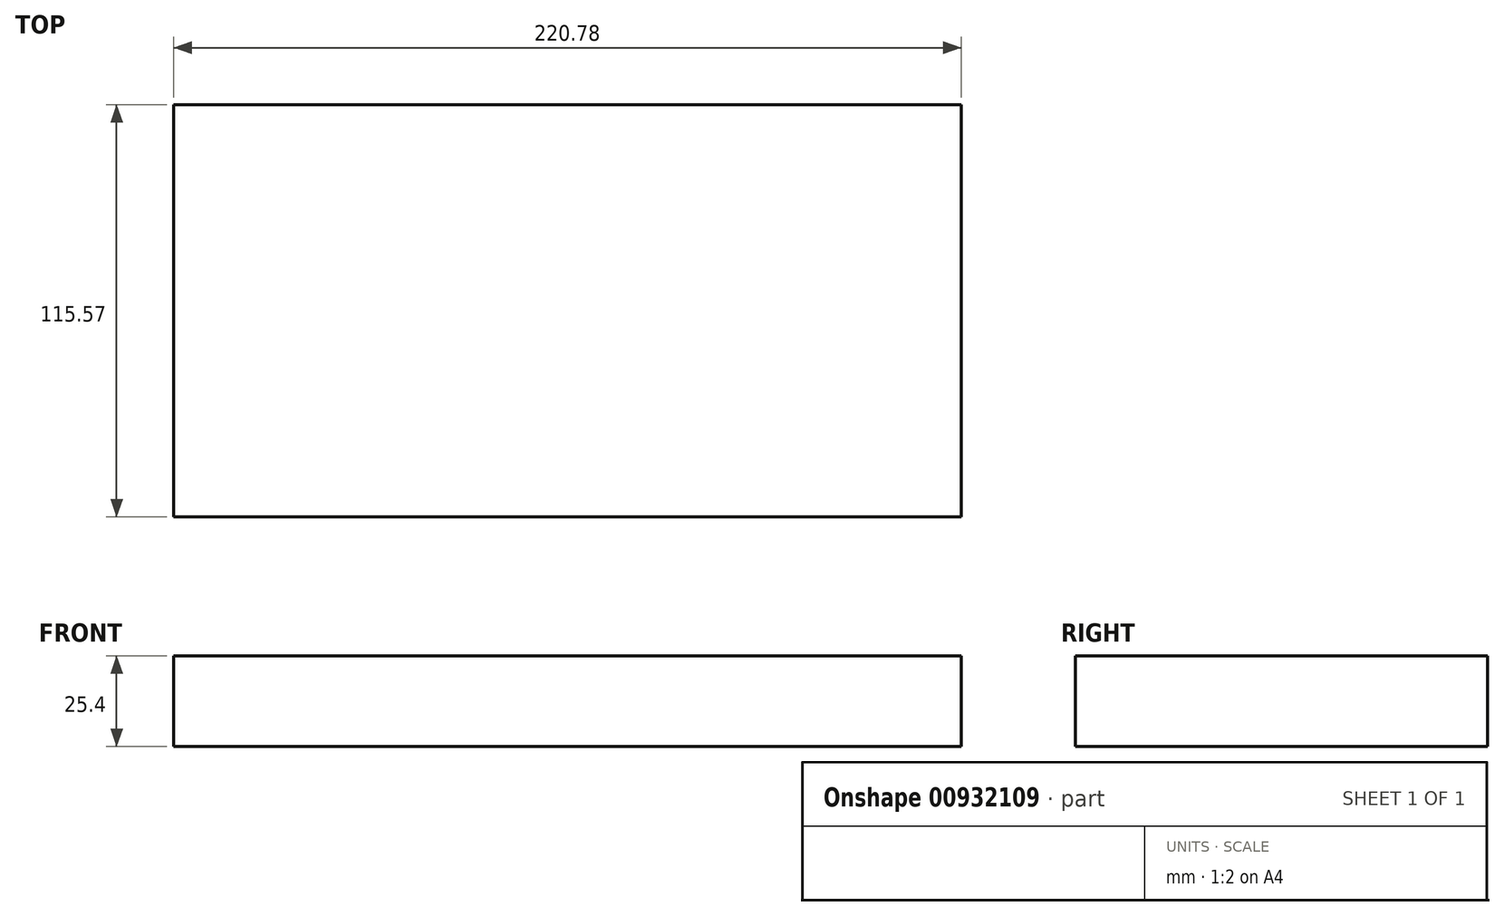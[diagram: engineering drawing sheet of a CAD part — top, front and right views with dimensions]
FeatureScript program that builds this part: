
annotation { "Feature Type Name" : "Feature", "Feature Type Description" : "" }
export const myFeature = defineFeature(function(context is Context, id is Id, definition is map)
    precondition{}
    {
        {
            var Q0;
            Q0=qCreatedBy(makeId("Top.planeOp"),FACE);
            var sketch = newSketch(context, id + "F0", { "sketchPlane" : qUnion([Q0])});
            skLineSegment(sketch, "E0.bottom", {"start": v(-126.23, 56.83) * mm, "end": v(94.55, 56.83) * mm});
            skLineSegment(sketch, "E0.top", {"start": v(-126.23, -58.74) * mm, "end": v(94.55, -58.74) * mm});
            skLineSegment(sketch, "E0.left", {"start": v(-126.23, 56.83) * mm, "end": v(-126.23, -58.74) * mm});
            skLineSegment(sketch, "E0.right", {"start": v(94.55, 56.83) * mm, "end": v(94.55, -58.74) * mm});
            skSolve(sketch);
        }
        {
            var Q0;
            Q0=makeQuery(id+"F0.imprint","IMPRINT",FACE,{"disambiguationData":[TD([[makeQuery(id+"F0.imprint","IMPRINT",EDGE,{"derivedFrom":sQuery(id+"F0.wireOp",EDGE,"E0.bottom")}),-1.0]])]});
            extrude(context, id + "F1", {"entities" : qUnion([Q0]), "depth" : 25.4 * mm, "offsetDistance" : 25.4 * mm});
        }
    });
